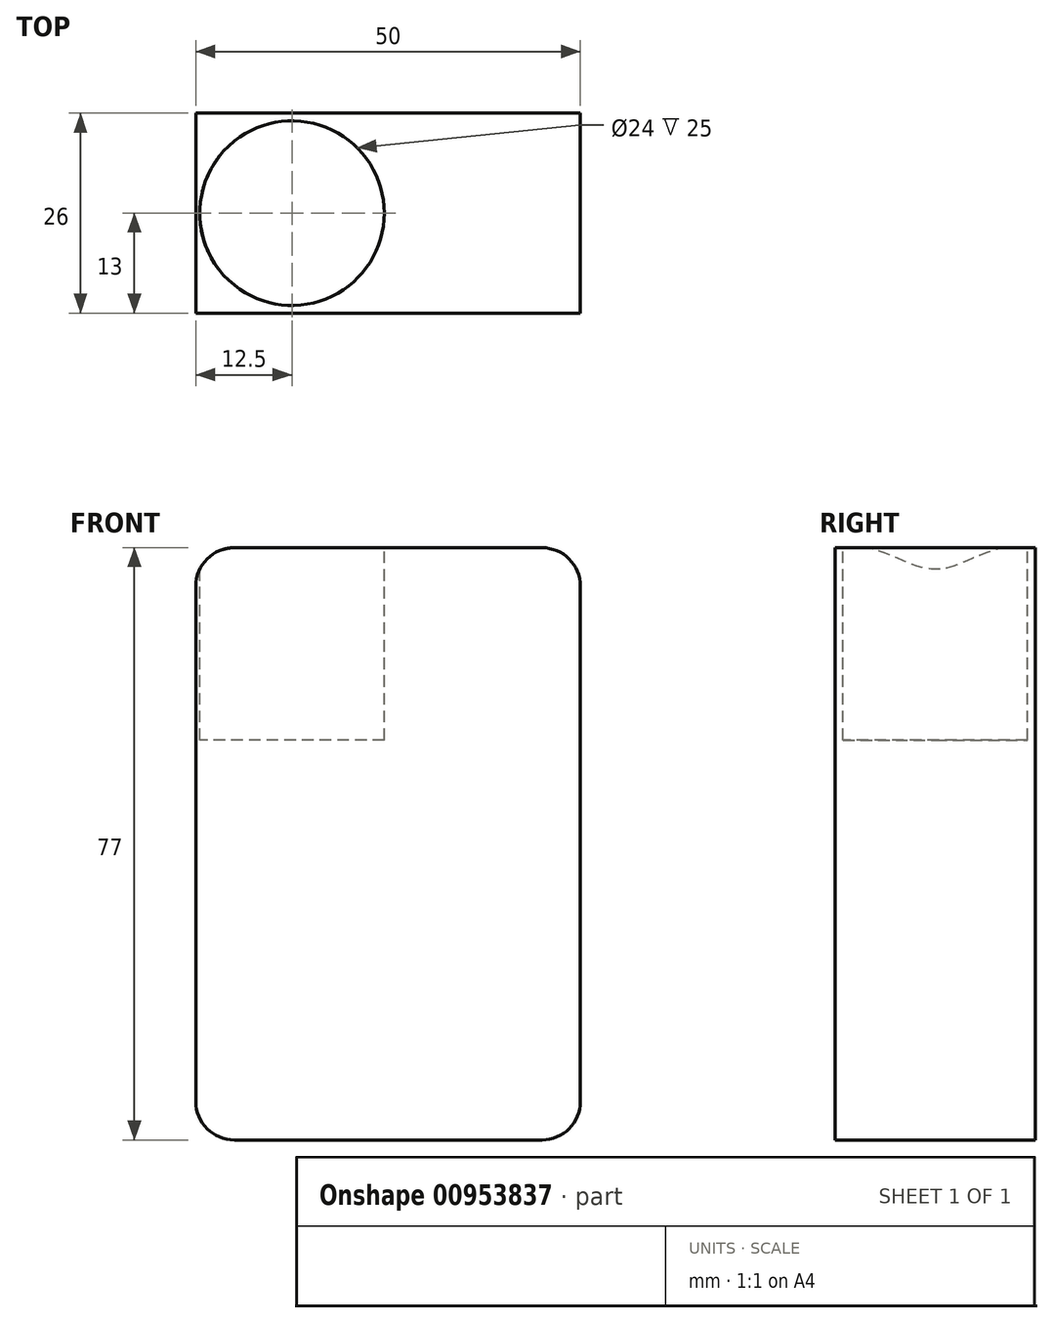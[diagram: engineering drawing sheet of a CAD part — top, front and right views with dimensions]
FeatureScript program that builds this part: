
annotation { "Feature Type Name" : "Feature", "Feature Type Description" : "" }
export const myFeature = defineFeature(function(context is Context, id is Id, definition is map)
    precondition{}
    {
        {
            var Q0;
            Q0=qCreatedBy(makeId("Top.planeOp"),FACE);
            var sketch = newSketch(context, id + "F0", { "sketchPlane" : qUnion([Q0])});
            skLineSegment(sketch, "E0.bottom", {"start": v(25, 13) * mm, "end": v(-25, 13) * mm});
            skLineSegment(sketch, "E0.top", {"start": v(25, -13) * mm, "end": v(-25, -13) * mm});
            skLineSegment(sketch, "E0.left", {"start": v(25, 13) * mm, "end": v(25, -13) * mm});
            skLineSegment(sketch, "E0.right", {"start": v(-25, 13) * mm, "end": v(-25, -13) * mm});
            skPoint(sketch, "E0.middle", {"position": v(0, 0) * mm});
            skSolve(sketch);
        }
        {
            var Q0;
            Q0=makeQuery(id+"F0.imprint","IMPRINT",FACE,{"disambiguationData":[TD([[makeQuery(id+"F0.imprint","IMPRINT",EDGE,{"derivedFrom":sQuery(id+"F0.wireOp",EDGE,"E0.bottom")}),1.0]])]});
            extrude(context, id + "F1", {"entities" : qUnion([Q0]), "depth" : 77 * mm, "offsetDistance" : 25 * mm});
        }
        {
            var Q0;
            Q0=makeQuery(id+"F1.opExtrude","CAP_EDGE",EDGE,{"disambiguationData":[OSD([sQuery(id+"F0.wireOp",EDGE,"E0.right")])],"isStart":true});
            var Q1;
            Q1=makeQuery(id+"F1.opExtrude","CAP_EDGE",EDGE,{"disambiguationData":[OSD([sQuery(id+"F0.wireOp",EDGE,"E0.left")])],"isStart":true});
            var Q2;
            Q2=makeQuery(id+"F1.opExtrude","CAP_EDGE",EDGE,{"disambiguationData":[OSD([sQuery(id+"F0.wireOp",EDGE,"E0.right")])],"isStart":false});
            var Q3;
            Q3=makeQuery(id+"F1.opExtrude","CAP_EDGE",EDGE,{"disambiguationData":[OSD([sQuery(id+"F0.wireOp",EDGE,"E0.left")])],"isStart":false});
            fillet(context, id + "F2", {"entities" : qUnion([Q0, Q1, Q2, Q3]), "radius" : 5 * mm, "tangentPropagation" : true, "allowEdgeOverflow" : false});
        }
        {
            var Q0;
            Q0=makeQuery(id+"F1.opExtrude","CAP_FACE",FACE,{"disambiguationData":[OSD([sQuery(id+"F0.wireOp",EDGE,"E0.bottom"),sQuery(id+"F0.wireOp",EDGE,"E0.top"),sQuery(id+"F0.wireOp",EDGE,"E0.left"),sQuery(id+"F0.wireOp",EDGE,"E0.right")])],"isStart":false});
            var sketch = newSketch(context, id + "F3", { "sketchPlane" : qUnion([Q0])});
            skLineSegment(sketch, "E1", {"start": v(0, 0) * mm, "end": v(-12.5, 0) * mm});
            skCircle(sketch, "E2", {"center": v(-12.5, 0) * mm, "radius": 12 * mm});
            skSolve(sketch);
        }
        {
            var Q0;
            {var subQ0=sQuery(id+"F3.wireOp",EDGE,"E2");var subQ1=makeQuery(id+"F3.imprint","IMPRINT",VERTEX,{"derivedFrom":subQ0});Q0=makeQuery(id+"F3.imprint","IMPRINT",FACE,{"disambiguationData":[TD([[makeQuery(id+"F3.imprint","IMPRINT",EDGE,{"disambiguationData":[TD([[subQ1,-1.0]])],"derivedFrom":subQ0}),1.0]])]});}
            var Q1;
            {var subQ0=sQuery(id+"F3.wireOp",EDGE,"E2");var subQ1=sQuery(id+"F0.wireOp",EDGE,"E0.right");var subQ2=makeQuery(id+"F2.opFillet","BLEND_EDGE",EDGE,{"blendedFrom":[makeQuery(id+"F1.opExtrude","CAP_EDGE",EDGE,{"disambiguationData":[OSD([subQ1])],"isStart":false}),makeQuery(id+"F1.opExtrude","CAP_FACE",FACE,{"disambiguationData":[OSD([sQuery(id+"F0.wireOp",EDGE,"E0.bottom"),sQuery(id+"F0.wireOp",EDGE,"E0.top"),sQuery(id+"F0.wireOp",EDGE,"E0.left"),subQ1])],"isStart":false})],"blendedInto":[makeQuery(id+"F1.opExtrude","CAP_FACE",FACE,{"disambiguationData":[OSD([sQuery(id+"F0.wireOp",EDGE,"E0.bottom"),sQuery(id+"F0.wireOp",EDGE,"E0.top"),sQuery(id+"F0.wireOp",EDGE,"E0.left"),subQ1])],"isStart":false})]});var subQ3=makeQuery(id+"F3.imprint","INTERSECT",VERTEX,{"disambiguationData":[OD(0.0)],"derivedFrom":[subQ2,subQ0]});Q1=makeQuery(id+"F3.imprint","IMPRINT",FACE,{"disambiguationData":[TD([[makeQuery(id+"F3.imprint","IMPRINT",EDGE,{"disambiguationData":[TD([[subQ3,-1.0]])],"derivedFrom":subQ0}),1.0]])]});}
            extrude(context, id + "F4", {"entities" : qUnion([Q0, Q1]), "operationType" : NewBodyOperationType.REMOVE, "oppositeDirection" : true, "depth" : 25 * mm, "offsetDistance" : 25 * mm});
        }
    });
